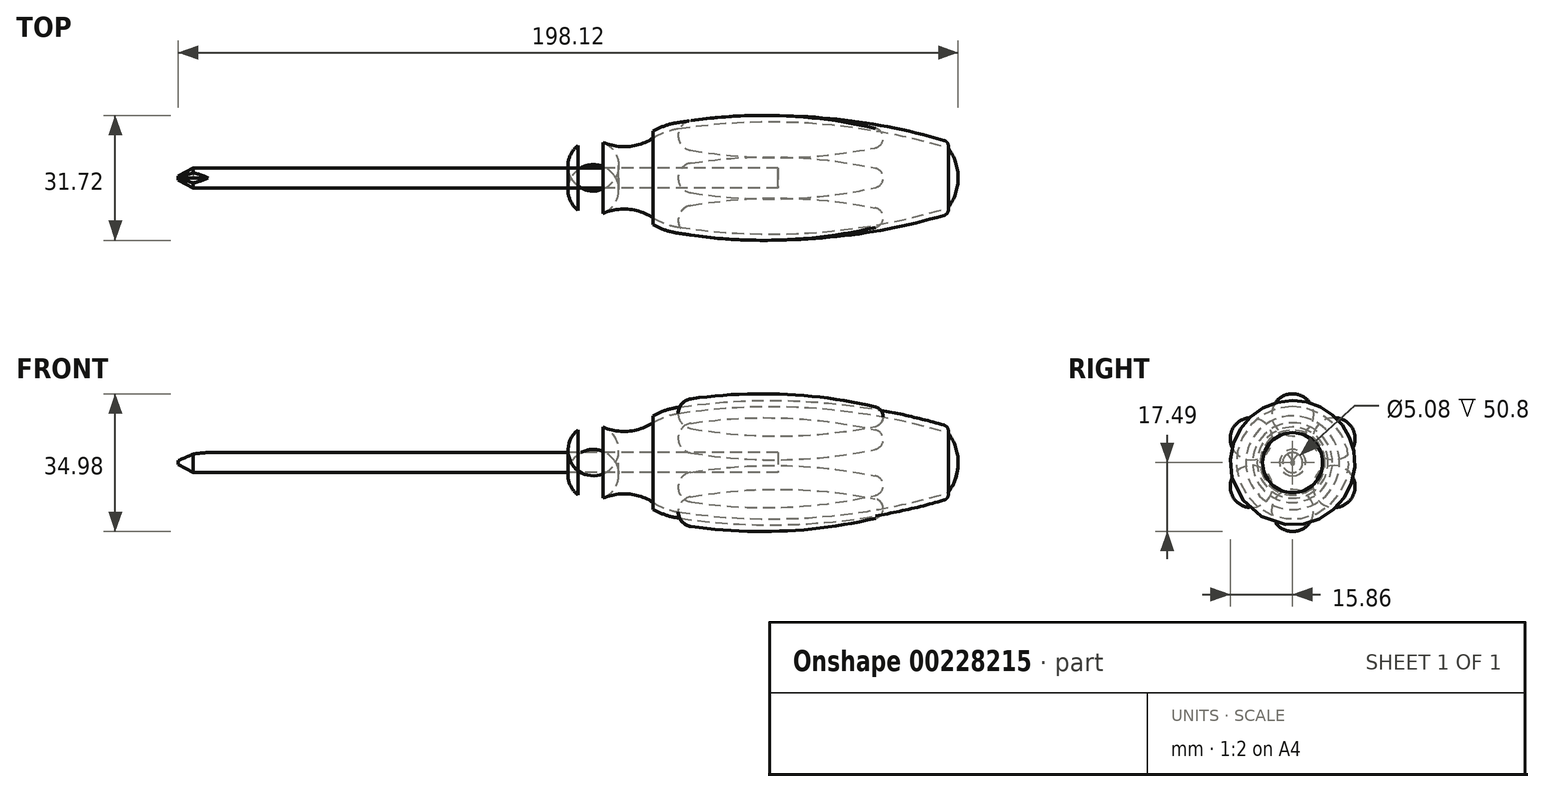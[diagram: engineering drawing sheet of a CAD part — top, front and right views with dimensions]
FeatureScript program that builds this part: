
annotation { "Feature Type Name" : "Feature", "Feature Type Description" : "" }
export const myFeature = defineFeature(function(context is Context, id is Id, definition is map)
    precondition{}
    {
        {
            var Q0;
            Q0=qCreatedBy(makeId("Front.planeOp"),FACE);
            var sketch = newSketch(context, id + "F0", { "sketchPlane" : qUnion([Q0])});
            skLineSegment(sketch, "E0", {"start": v(-101.6, 0) * mm, "end": v(96.52, 0) * mm});
            skLineSegment(sketch, "E1", {"start": v(96.52, 0) * mm, "end": v(117.55, 0) * mm, "construction": true});
            skLineSegment(sketch, "E2", {"start": v(50.8, 2.54) * mm, "end": v(-97.8, 2.54) * mm});
            skLineSegment(sketch, "E3", {"start": v(-101.6, 0.5) * mm, "end": v(-101.6, 0) * mm});
            skLineSegment(sketch, "E4", {"start": v(0, 2.54) * mm, "end": v(0, 8.25) * mm});
            skArc(sketch, "E5", {"start": v(6.35, 9.02) * mm, "mid": v(3.07, 9.48) * mm, "end": v(0, 8.25) * mm});
            skArc(sketch, "E6", {"start": v(6.35, 9.02) * mm, "mid": v(12.84, 7.99) * mm, "end": v(19.05, 10.11) * mm});
            skArc(sketch, "E7", {"start": v(25.4, 12.52) * mm, "mid": v(22.1, 11.65) * mm, "end": v(19.05, 10.11) * mm});
            skArc(sketch, "E8", {"start": v(93.98, 7.62) * mm, "mid": v(59.96, 13.9) * mm, "end": v(25.4, 12.52) * mm});
            skArc(sketch, "E9", {"start": v(96.52, 0) * mm, "mid": v(95.87, 4.02) * mm, "end": v(93.98, 7.62) * mm});
            skArc(sketch, "E10.0", {"start": v(25.17, 14.02) * mm, "mid": v(22.01, 13.24) * mm, "end": v(19.05, 11.9) * mm});
            skArc(sketch, "E10.1", {"start": v(92.95, 9.52) * mm, "mid": v(59.3, 15.46) * mm, "end": v(25.17, 14.02) * mm});
            skLineSegment(sketch, "E11", {"start": v(19.05, 11.9) * mm, "end": v(19.05, 10.11) * mm});
            skArc(sketch, "E12", {"start": v(93.98, 7.62) * mm, "mid": v(93.86, 8.78) * mm, "end": v(92.95, 9.52) * mm});
            skPoint(sketch, "E13.orphan", {"position": v(0, 0) * mm});
            skLineSegment(sketch, "E14", {"start": v(50.8, 2.54) * mm, "end": v(50.8, 0) * mm});
            skLineSegment(sketch, "E15", {"start": v(-101.6, 0.5) * mm, "end": v(-97.8, 2.54) * mm});
            skPoint(sketch, "E16.orphan", {"position": v(-101.6, 2.54) * mm});
            skSolve(sketch);
        }
        {
            var Q0;
            Q0=qCreatedBy(makeId("Front.planeOp"),FACE);
            var sketch = newSketch(context, id + "F1", { "sketchPlane" : qUnion([Q0])});
            skLineSegment(sketch, "E17", {"start": v(25.4, 12.52) * mm, "end": v(77.47, 11.64) * mm});
            skArc(sketch, "E18", {"start": v(28.67, 16.22) * mm, "mid": v(26.35, 14.97) * mm, "end": v(25.4, 12.52) * mm});
            skArc(sketch, "E19", {"start": v(77.47, 11.64) * mm, "mid": v(76.93, 13.25) * mm, "end": v(75.5, 14.16) * mm});
            skArc(sketch, "E20", {"start": v(75.5, 14.16) * mm, "mid": v(52.19, 17.37) * mm, "end": v(28.67, 16.22) * mm});
            skSolve(sketch);
        }
        {
            var Q0;
            Q0=qCreatedBy(makeId("Front.planeOp"),FACE);
            var sketch = newSketch(context, id + "F2", { "sketchPlane" : qUnion([Q0])});
            skLineSegment(sketch, "E21", {"start": v(-101.6, 0.5) * mm, "end": v(-93.98, 2.54) * mm});
            skSolve(sketch);
        }
        {
            var Q0;
            Q0=sQuery(id+"F2.wireOp",VERTEX,"E21.start");
            var Q1;
            Q1=sQuery(id+"F2.wireOp",EDGE,"E21");
            cPlane(context, id + "F3", {"entities" : qUnion([Q0, Q1]), "cplaneType" : CPlaneType.LINE_POINT, "offset" : 25.4 * mm, "width" : 152.4 * mm, "height" : 152.4 * mm});
        }
        {
            var Q0;
            Q0=qCreatedBy(id+"F3.planeOp",FACE);
            var sketch = newSketch(context, id + "F4", { "sketchPlane" : qUnion([Q0])});
            skLineSegment(sketch, "E22", {"start": v(5.08, 29.2) * mm, "end": v(0, 26.67) * mm});
            skLineSegment(sketch, "E23", {"start": v(0, 26.67) * mm, "end": v(-5.08, 29.2) * mm});
            skLineSegment(sketch, "E24", {"start": v(-5.08, 29.2) * mm, "end": v(5.08, 29.2) * mm});
            skLineSegment(sketch, "E25", {"start": v(0, 29.2) * mm, "end": v(0, 26.67) * mm, "construction": true});
            skSolve(sketch);
        }
        {
            var Q0;
            {var subQ0=sQuery(id+"F0.wireOp",EDGE,"E3");Q0=makeQuery(id+"F0.imprint","IMPRINT",FACE,{"disambiguationData":[TD([[makeQuery(id+"F0.imprint","IMPRINT",EDGE,{"derivedFrom":subQ0}),1.0]])]});}
            var Q1;
            Q1=sQuery(id+"F0.wireOp",EDGE,"E0");
            revolve(context, id + "F5", {"entities" : qUnion([Q0]), "axis" : qUnion([Q1]), "revolveType" : RevolveType.FULL});
        }
        {
            var Q0;
            {var subQ0=sQuery(id+"F0.wireOp",EDGE,"E4");Q0=makeQuery(id+"F0.imprint","IMPRINT",FACE,{"disambiguationData":[TD([[makeQuery(id+"F0.imprint","IMPRINT",EDGE,{"derivedFrom":subQ0}),-1.0]])]});}
            var Q1;
            Q1=sQuery(id+"F0.wireOp",EDGE,"E1");
            revolve(context, id + "F6", {"entities" : qUnion([Q0]), "axis" : qUnion([Q1]), "revolveType" : RevolveType.FULL});
        }
        {
            var Q0;
            Q0=makeQuery(id+"F0.imprint","IMPRINT",FACE,{"disambiguationData":[TD([[makeQuery(id+"F0.imprint","IMPRINT",EDGE,{"derivedFrom":sQuery(id+"F0.wireOp",EDGE,"E7")}),-1.0]])]});
            var Q1;
            Q1=sQuery(id+"F0.wireOp",EDGE,"E1");
            revolve(context, id + "F7", {"entities" : qUnion([Q0]), "axis" : qUnion([Q1]), "revolveType" : RevolveType.FULL});
        }
        {
            var Q0;
            Q0=makeQuery(id+"F1.imprint","IMPRINT",FACE,{"disambiguationData":[TD([[makeQuery(id+"F1.imprint","IMPRINT",EDGE,{"derivedFrom":sQuery(id+"F1.wireOp",EDGE,"E17")}),1.0]])]});
            var Q1;
            Q1=sQuery(id+"F1.wireOp",EDGE,"E17");
            revolve(context, id + "F8", {"entities" : qUnion([Q0]), "axis" : qUnion([Q1]), "revolveType" : RevolveType.FULL});
        }
        {
            var Q0;
            Q0=makeQuery(id+"F8.opRevolve","SWEPT_BODY",BODY,{"disambiguationData":[OSD([sQuery(id+"F1.wireOp",EDGE,"E17"),sQuery(id+"F1.wireOp",EDGE,"E18"),sQuery(id+"F1.wireOp",EDGE,"E19"),sQuery(id+"F1.wireOp",EDGE,"E20")])]});
            var Q1;
            Q1=sQuery(id+"F0.wireOp",EDGE,"E1");
            circularPattern(context, id + "F9", {"entities" : qUnion([Q0]), "axis" : qUnion([Q1]), "angle" : 360 * degree, "instanceCount" : 6, "equalSpace" : true});
        }
        {
            var Q0;
            Q0=makeQuery(id+"F6.opRevolve","SWEPT_BODY",BODY,{"disambiguationData":[OSD([sQuery(id+"F0.wireOp",EDGE,"E0"),sQuery(id+"F0.wireOp",EDGE,"E2"),sQuery(id+"F0.wireOp",EDGE,"E4"),sQuery(id+"F0.wireOp",EDGE,"E5"),sQuery(id+"F0.wireOp",EDGE,"E6"),sQuery(id+"F0.wireOp",EDGE,"E7"),sQuery(id+"F0.wireOp",EDGE,"E8"),sQuery(id+"F0.wireOp",EDGE,"E9"),sQuery(id+"F0.wireOp",EDGE,"E14")])]});
            var Q1;
            Q1=makeQuery(id+"F7.opRevolve","SWEPT_BODY",BODY,{"disambiguationData":[OSD([sQuery(id+"F0.wireOp",EDGE,"E7"),sQuery(id+"F0.wireOp",EDGE,"E8"),sQuery(id+"F0.wireOp",EDGE,"E10.0"),sQuery(id+"F0.wireOp",EDGE,"E10.1"),sQuery(id+"F0.wireOp",EDGE,"E11"),sQuery(id+"F0.wireOp",EDGE,"E12")])]});
            booleanBodies(context, id + "F10", {"operationType" : BooleanOperationType.SUBTRACTION, "tools" : qUnion([Q0]), "targets" : qUnion([Q1]), "keepTools" : true});
        }
        {
            var Q0;
            Q0=makeQuery(id+"F4.imprint","IMPRINT",FACE,{"disambiguationData":[TD([[makeQuery(id+"F4.imprint","IMPRINT",EDGE,{"derivedFrom":sQuery(id+"F4.wireOp",EDGE,"E22")}),-1.0]])]});
            var Q1;
            Q1=sQuery(id+"F2.wireOp",EDGE,"E21");
            sweep(context, id + "F11", {"operationType" : NewBodyOperationType.REMOVE, "profiles" : qUnion([Q0]), "path" : qUnion([Q1])});
        }
    });
